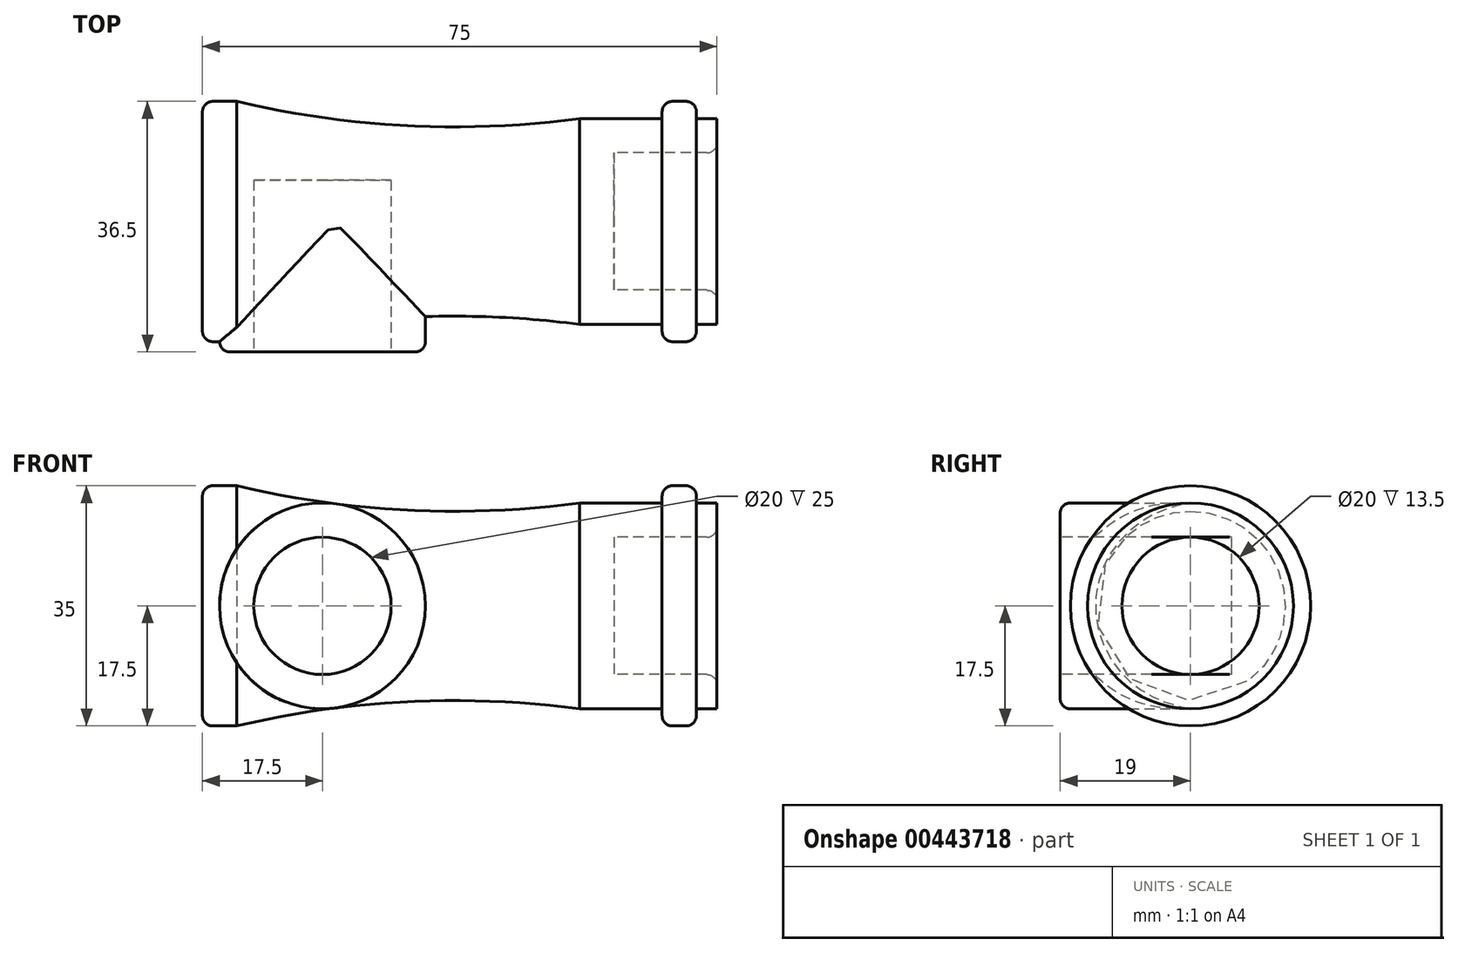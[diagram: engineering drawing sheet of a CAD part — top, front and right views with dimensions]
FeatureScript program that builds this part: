
annotation { "Feature Type Name" : "Feature", "Feature Type Description" : "" }
export const myFeature = defineFeature(function(context is Context, id is Id, definition is map)
    precondition{}
    {
        {
            var Q0;
            Q0=qCreatedBy(makeId("Front.planeOp"),FACE);
            var sketch = newSketch(context, id + "F0", { "sketchPlane" : qUnion([Q0])});
            skLineSegment(sketch, "E0", {"start": v(0, 0) * mm, "end": v(0, 17.5) * mm});
            skLineSegment(sketch, "E1", {"start": v(0, 17.5) * mm, "end": v(5, 17.5) * mm});
            skLineSegment(sketch, "E2", {"start": v(0, 0) * mm, "end": v(60, 0) * mm});
            skLineSegment(sketch, "E3", {"start": v(60, 0) * mm, "end": v(60, 10) * mm});
            skLineSegment(sketch, "E4", {"start": v(60, 10) * mm, "end": v(75, 10) * mm});
            skLineSegment(sketch, "E5", {"start": v(75, 10) * mm, "end": v(75, 15) * mm});
            skLineSegment(sketch, "E6", {"start": v(75, 15) * mm, "end": v(72, 15) * mm});
            skLineSegment(sketch, "E7", {"start": v(72, 15) * mm, "end": v(72, 17.5) * mm});
            skLineSegment(sketch, "E8", {"start": v(72, 17.5) * mm, "end": v(67, 17.5) * mm});
            skLineSegment(sketch, "E9", {"start": v(67, 17.5) * mm, "end": v(67, 15) * mm});
            skArc(sketch, "E10", {"start": v(5, 17.5) * mm, "mid": v(29.89, 13.96) * mm, "end": v(55, 15) * mm});
            skLineSegment(sketch, "E11", {"start": v(55, 15) * mm, "end": v(67, 15) * mm});
            skSolve(sketch);
        }
        {
            var Q0;
            Q0 = qSketchRegion(id + "F0", true);
            var Q1;
            Q1=sQuery(id+"F0.wireOp",EDGE,"E2");
            revolve(context, id + "F1", {"entities" : qUnion([Q0]), "axis" : qUnion([Q1]), "revolveType" : RevolveType.FULL});
        }
        {
            var Q0;
            Q0=qCreatedBy(makeId("Front.planeOp"),FACE);
            var sketch = newSketch(context, id + "F2", { "sketchPlane" : qUnion([Q0])});
            skCircle(sketch, "E12", {"center": v(17.5, 0) * mm, "radius": 15 * mm});
            skSolve(sketch);
        }
        {
            var Q0;
            Q0 = qSketchRegion(id + "F2", true);
            extrude(context, id + "F3", {"entities" : qUnion([Q0]), "operationType" : NewBodyOperationType.ADD, "depth" : 19 * mm});
        }
        {
            var Q0;
            Q0=makeQuery(id+"F3.opExtrude","CAP_FACE",FACE,{"disambiguationData":[OSD([sQuery(id+"F2.wireOp",EDGE,"E12")])],"isStart":false});
            var sketch = newSketch(context, id + "F4", { "sketchPlane" : qUnion([Q0])});
            skCircle(sketch, "E13", {"center": v(17.5, 0) * mm, "radius": 10 * mm});
            skSolve(sketch);
        }
        {
            var Q0;
            Q0 = qSketchRegion(id + "F4", true);
            extrude(context, id + "F5", {"entities" : qUnion([Q0]), "operationType" : NewBodyOperationType.REMOVE, "oppositeDirection" : true, "depth" : 25 * mm});
        }
        {
            var Q0;
            Q0=makeQuery(id+"F1.opRevolve","SWEPT_EDGE",EDGE,{"disambiguationData":[OSD([sQuery(id+"F0.wireOp",EDGE,"E0"),sQuery(id+"F0.wireOp",EDGE,"E1")])]});
            var Q1;
            Q1=makeQuery(id+"F3.opExtrude","CAP_EDGE",EDGE,{"disambiguationData":[OSD([sQuery(id+"F2.wireOp",EDGE,"E12")])],"isStart":false});
            var Q2;
            Q2=makeQuery(id+"F1.opRevolve","SWEPT_EDGE",EDGE,{"disambiguationData":[OSD([sQuery(id+"F0.wireOp",EDGE,"E4"),sQuery(id+"F0.wireOp",EDGE,"E5")])]});
            var Q3;
            Q3=makeQuery(id+"F1.opRevolve","SWEPT_EDGE",EDGE,{"disambiguationData":[OSD([sQuery(id+"F0.wireOp",EDGE,"E8"),sQuery(id+"F0.wireOp",EDGE,"E9")])]});
            var Q4;
            Q4=makeQuery(id+"F1.opRevolve","SWEPT_EDGE",EDGE,{"disambiguationData":[OSD([sQuery(id+"F0.wireOp",EDGE,"E7"),sQuery(id+"F0.wireOp",EDGE,"E8")])]});
            fillet(context, id + "F6", {"entities" : qUnion([Q0, Q1, Q2, Q3, Q4]), "radius" : 1.5 * mm, "tangentPropagation" : true, "allowEdgeOverflow" : false});
        }
    });
